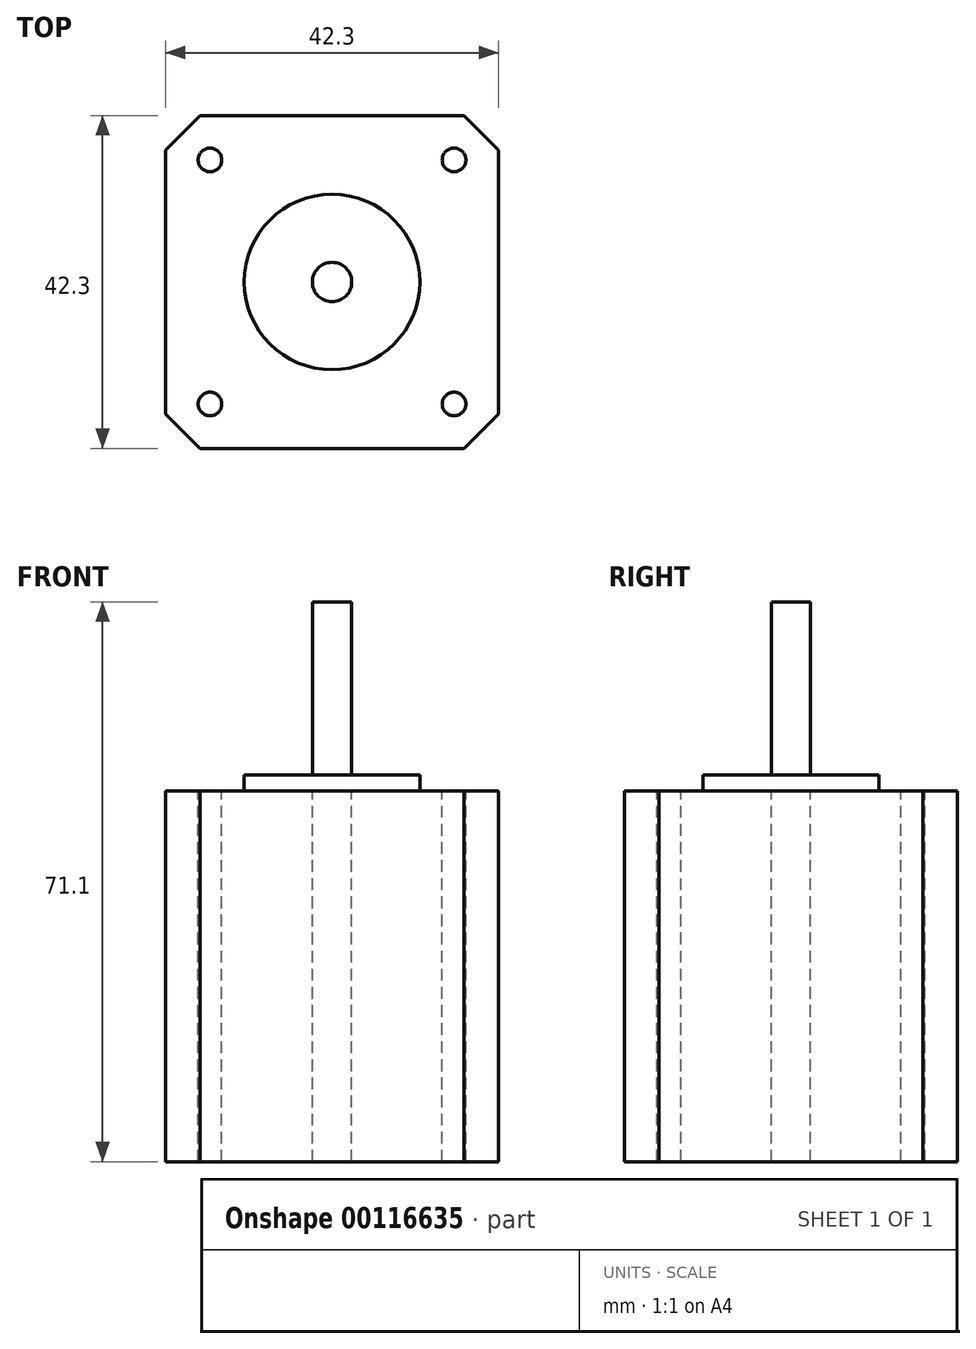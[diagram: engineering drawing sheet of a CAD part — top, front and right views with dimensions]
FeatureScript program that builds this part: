
annotation { "Feature Type Name" : "Feature", "Feature Type Description" : "" }
export const myFeature = defineFeature(function(context is Context, id is Id, definition is map)
    precondition{}
    {
        {
            var Q0;
            Q0=qCreatedBy(makeId("Top.planeOp"),FACE);
            var sketch = newSketch(context, id + "F0", { "sketchPlane" : qUnion([Q0])});
            skLineSegment(sketch, "E0.bottom", {"start": v(21.15, -21.15) * mm, "end": v(-21.15, -21.15) * mm, "construction": true});
            skLineSegment(sketch, "E0.top", {"start": v(21.15, 21.15) * mm, "end": v(-21.15, 21.15) * mm, "construction": true});
            skLineSegment(sketch, "E0.left", {"start": v(21.15, -21.15) * mm, "end": v(21.15, 21.15) * mm, "construction": true});
            skLineSegment(sketch, "E0.right", {"start": v(-21.15, -21.15) * mm, "end": v(-21.15, 21.15) * mm, "construction": true});
            skPoint(sketch, "E0.middle", {"position": v(0, 0) * mm});
            skLineSegment(sketch, "E1", {"start": v(-21.15, 16.75) * mm, "end": v(-21.15, -16.75) * mm});
            skPoint(sketch, "E2", {"position": v(-21.15, 0) * mm});
            skLineSegment(sketch, "E3", {"start": v(0, 21.15) * mm, "end": v(0, -21.15) * mm, "construction": true});
            skLineSegment(sketch, "E4.MirrorCS", {"start": v(21.15, 16.75) * mm, "end": v(21.15, -16.75) * mm});
            skLineSegment(sketch, "E5", {"start": v(-16.75, 21.15) * mm, "end": v(16.75, 21.15) * mm});
            skPoint(sketch, "E6", {"position": v(0, 21.15) * mm});
            skLineSegment(sketch, "E7", {"start": v(-21.15, 0) * mm, "end": v(21.15, 0) * mm, "construction": true});
            skLineSegment(sketch, "E8.MirrorCS", {"start": v(-16.75, -21.15) * mm, "end": v(16.75, -21.15) * mm});
            skLineSegment(sketch, "E9", {"start": v(-21.15, 16.75) * mm, "end": v(-16.75, 21.15) * mm});
            skLineSegment(sketch, "E10", {"start": v(16.75, 21.15) * mm, "end": v(21.15, 16.75) * mm});
            skLineSegment(sketch, "E11", {"start": v(21.15, -16.75) * mm, "end": v(16.75, -21.15) * mm});
            skLineSegment(sketch, "E12", {"start": v(-16.75, -21.15) * mm, "end": v(-21.15, -16.75) * mm});
            skCircle(sketch, "E13", {"center": v(0, 0) * mm, "radius": 11.15 * mm});
            skCircle(sketch, "E14", {"center": v(0, 0) * mm, "radius": 2.5 * mm});
            skCircle(sketch, "E15", {"center": v(15.5, 15.5) * mm, "radius": 1.5 * mm});
            skCircle(sketch, "E16.MirrorC", {"center": v(15.5, -15.5) * mm, "radius": 1.5 * mm});
            skCircle(sketch, "E17.MirrorC", {"center": v(-15.5, 15.5) * mm, "radius": 1.5 * mm});
            skCircle(sketch, "E18.MirrorC", {"center": v(-15.5, -15.5) * mm, "radius": 1.5 * mm});
            skLineSegment(sketch, "E19", {"start": v(-15.5, 15.5) * mm, "end": v(15.5, 15.5) * mm, "construction": true});
            skLineSegment(sketch, "E20", {"start": v(-15.5, 15.5) * mm, "end": v(-15.5, -15.5) * mm, "construction": true});
            skSolve(sketch);
        }
        {
            var Q0;
            Q0 = qSketchRegion(id + "F0", true);
            var Q1;
            Q1=makeQuery(id+"F0.imprint","IMPRINT",FACE,{"disambiguationData":[TD([[makeQuery(id+"F0.imprint","IMPRINT",EDGE,{"derivedFrom":sQuery(id+"F0.wireOp",EDGE,"E13")}),1.0]])]});
            extrude(context, id + "F1", {"entities" : qUnion([Q0, Q1]), "oppositeDirection" : true, "depth" : 47.1 * mm});
        }
        {
            var Q0;
            Q0=makeQuery(id+"F0.imprint","IMPRINT",FACE,{"disambiguationData":[TD([[makeQuery(id+"F0.imprint","IMPRINT",EDGE,{"derivedFrom":sQuery(id+"F0.wireOp",EDGE,"E13")}),1.0]])]});
            extrude(context, id + "F2", {"entities" : qUnion([Q0]), "operationType" : NewBodyOperationType.ADD, "depth" : 2 * mm});
        }
        {
            var Q0;
            Q0=makeQuery(id+"F0.imprint","IMPRINT",FACE,{"disambiguationData":[TD([[makeQuery(id+"F0.imprint","IMPRINT",EDGE,{"derivedFrom":sQuery(id+"F0.wireOp",EDGE,"E14")}),1.0]])]});
            extrude(context, id + "F3", {"entities" : qUnion([Q0]), "operationType" : NewBodyOperationType.ADD, "depth" : 24 * mm});
        }
    });
